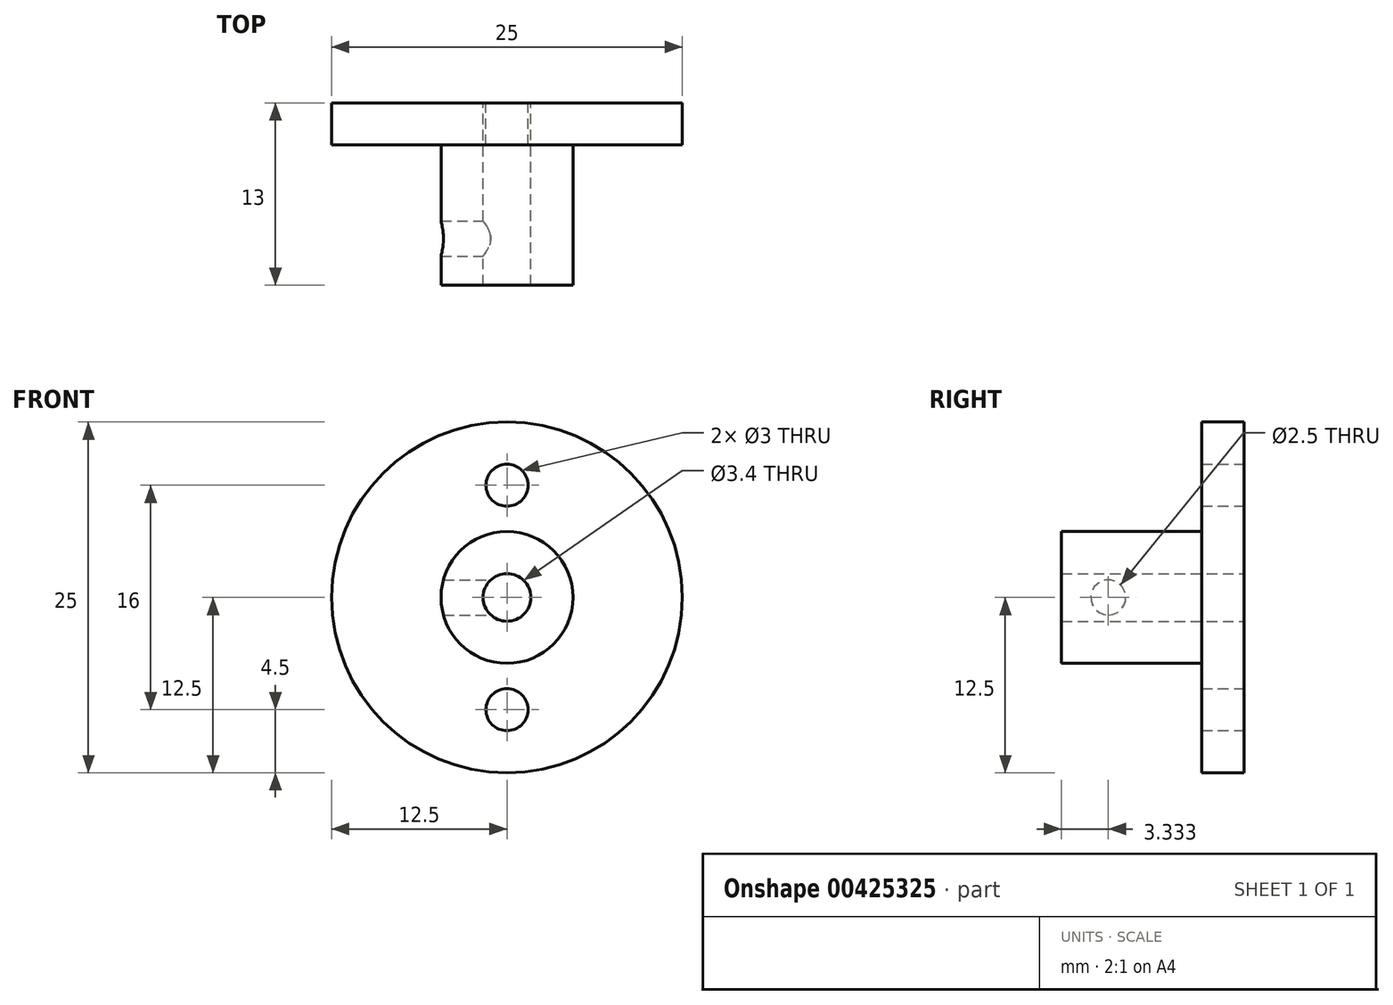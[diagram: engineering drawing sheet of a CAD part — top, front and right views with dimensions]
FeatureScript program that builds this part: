
annotation { "Feature Type Name" : "Feature", "Feature Type Description" : "" }
export const myFeature = defineFeature(function(context is Context, id is Id, definition is map)
    precondition{}
    {
        {
            assignVariable(context, id + "F0", {"name" : "setScrewExtrude", "anyValue" : 10 * mm});
        }
        {
            assignVariable(context, id + "F1", {"name" : "rivetExtrude", "anyValue" : 3 * mm});
        }
        {
            var Q0;
            Q0=qCreatedBy(makeId("Front.planeOp"),FACE);
            var sketch = newSketch(context, id + "F2", { "sketchPlane" : qUnion([Q0])});
            skCircle(sketch, "E0", {"center": v(0, 0) * mm, "radius": 12.5 * mm});
            skCircle(sketch, "E1", {"center": v(0, 0) * mm, "radius": 1.7 * mm});
            skCircle(sketch, "E2", {"center": v(0, 8) * mm, "radius": 1.5 * mm});
            skCircle(sketch, "E3", {"center": v(0, -8) * mm, "radius": 1.5 * mm});
            skSolve(sketch);
        }
        {
            var Q0;
            Q0 = qSketchRegion(id + "F2", true);
            extrude(context, id + "F3", {"entities" : qUnion([Q0]), "depth" : getVariable(context, 'rivetExtrude'), "offsetDistance" : 25 * mm});
        }
        {
            var Q0;
            Q0=makeQuery(id+"F3.opExtrude","CAP_FACE",FACE,{"disambiguationData":[OSD([sQuery(id+"F2.wireOp",EDGE,"E0"),sQuery(id+"F2.wireOp",EDGE,"E1"),sQuery(id+"F2.wireOp",EDGE,"E2"),sQuery(id+"F2.wireOp",EDGE,"E3")])],"isStart":false});
            var sketch = newSketch(context, id + "F4", { "sketchPlane" : qUnion([Q0])});
            skCircle(sketch, "E4", {"center": v(0, 0) * mm, "radius": 1.7 * mm});
            skCircle(sketch, "E5", {"center": v(0, 0) * mm, "radius": 4.7 * mm});
            skSolve(sketch);
        }
        {
            var Q0;
            Q0 = qSketchRegion(id + "F4", true);
            extrude(context, id + "F5", {"entities" : qUnion([Q0]), "operationType" : NewBodyOperationType.ADD, "depth" : getVariable(context, 'setScrewExtrude'), "offsetDistance" : 25 * mm});
        }
        {
            var Q0;
            Q0=qCreatedBy(makeId("Right.planeOp"),FACE);
            var sketch = newSketch(context, id + "F6", { "sketchPlane" : qUnion([Q0])});
            skCircle(sketch, "E6", {"center": v(-9.67, 0) * mm, "radius": 1.25 * mm});
            skSolve(sketch);
        }
        {
            var Q0;
            Q0 = qSketchRegion(id + "F6", true);
            extrude(context, id + "F7", {"entities" : qUnion([Q0]), "operationType" : NewBodyOperationType.REMOVE, "oppositeDirection" : true, "depth" : 25 * mm, "offsetDistance" : 25 * mm});
        }
    });
